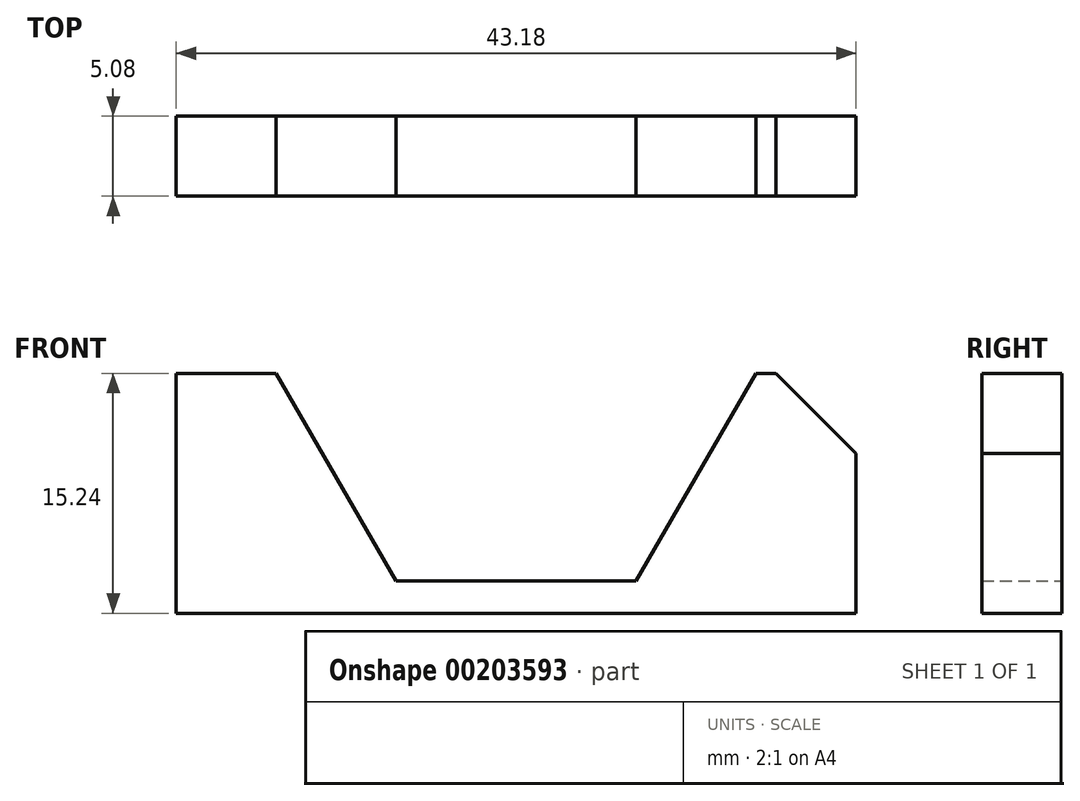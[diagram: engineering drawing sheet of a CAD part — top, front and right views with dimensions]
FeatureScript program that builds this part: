
annotation { "Feature Type Name" : "Feature", "Feature Type Description" : "" }
export const myFeature = defineFeature(function(context is Context, id is Id, definition is map)
    precondition{}
    {
        {
            var Q0;
            Q0=qCreatedBy(makeId("Front.planeOp"),FACE);
            var sketch = newSketch(context, id + "F0", { "sketchPlane" : qUnion([Q0])});
            skLineSegment(sketch, "E0.2", {"start": v(36.83, 0) * mm, "end": v(29.21, -13.2) * mm});
            skLineSegment(sketch, "E0.3", {"start": v(29.21, -13.2) * mm, "end": v(13.97, -13.2) * mm});
            skLineSegment(sketch, "E0.4", {"start": v(13.97, -13.2) * mm, "end": v(6.35, 0) * mm});
            skLineSegment(sketch, "E1", {"start": v(6.35, 0) * mm, "end": v(0, 0) * mm});
            skLineSegment(sketch, "E2", {"start": v(36.83, 0) * mm, "end": v(43.18, 0) * mm});
            skLineSegment(sketch, "E3", {"start": v(43.18, 0) * mm, "end": v(43.18, -15.24) * mm});
            skLineSegment(sketch, "E4", {"start": v(43.18, -15.24) * mm, "end": v(0, -15.24) * mm});
            skLineSegment(sketch, "E5.MirrorCS", {"start": v(-43.18, -15.24) * mm, "end": v(0, -15.24) * mm});
            skLineSegment(sketch, "E6.MirrorCS", {"start": v(-36.83, 0) * mm, "end": v(-43.18, 0) * mm});
            skLineSegment(sketch, "E7.MirrorCS", {"start": v(-6.35, 0) * mm, "end": v(0, 0) * mm});
            skLineSegment(sketch, "E8.MirrorCS", {"start": v(-29.21, -13.2) * mm, "end": v(-13.97, -13.2) * mm});
            skLineSegment(sketch, "E9.MirrorCS", {"start": v(-43.18, 0) * mm, "end": v(-43.18, -15.24) * mm});
            skLineSegment(sketch, "E10.MirrorCS", {"start": v(-36.83, 0) * mm, "end": v(-29.21, -13.2) * mm});
            skLineSegment(sketch, "E11.MirrorCS", {"start": v(-13.97, -13.2) * mm, "end": v(-6.35, 0) * mm});
            skSolve(sketch);
        }
        {
            var Q0;
            Q0=makeQuery(id+"F0.imprint","IMPRINT",FACE,{"disambiguationData":[TD([[makeQuery(id+"F0.imprint","IMPRINT",EDGE,{"derivedFrom":sQuery(id+"F0.wireOp",EDGE,"E0.2")}),1.0]])]});
            extrude(context, id + "F1", {"entities" : qUnion([Q0]), "depth" : 116.84 * mm});
        }
        {
            var Q0;
            Q0=makeQuery(id+"F1.opExtrude","CAP_FACE",FACE,{"disambiguationData":[OSD([sQuery(id+"F0.wireOp",EDGE,"E0.2"),sQuery(id+"F0.wireOp",EDGE,"E0.3"),sQuery(id+"F0.wireOp",EDGE,"E0.4"),sQuery(id+"F0.wireOp",EDGE,"E1"),sQuery(id+"F0.wireOp",EDGE,"E2"),sQuery(id+"F0.wireOp",EDGE,"E3"),sQuery(id+"F0.wireOp",EDGE,"E4"),sQuery(id+"F0.wireOp",EDGE,"E5.MirrorCS"),sQuery(id+"F0.wireOp",EDGE,"E6.MirrorCS"),sQuery(id+"F0.wireOp",EDGE,"E7.MirrorCS"),sQuery(id+"F0.wireOp",EDGE,"E8.MirrorCS"),sQuery(id+"F0.wireOp",EDGE,"E9.MirrorCS"),sQuery(id+"F0.wireOp",EDGE,"E10.MirrorCS"),sQuery(id+"F0.wireOp",EDGE,"E11.MirrorCS")])],"isStart":false});
            var sketch = newSketch(context, id + "F2", { "sketchPlane" : qUnion([Q0])});
            skLineSegment(sketch, "E12.bottom", {"start": v(-43.18, 0) * mm, "end": v(43.18, 0) * mm});
            skLineSegment(sketch, "E12.top", {"start": v(-43.18, -15.24) * mm, "end": v(43.18, -15.24) * mm});
            skLineSegment(sketch, "E12.left", {"start": v(-43.18, 0) * mm, "end": v(-43.18, -15.24) * mm});
            skLineSegment(sketch, "E12.right", {"start": v(43.18, 0) * mm, "end": v(43.18, -15.24) * mm});
            skSolve(sketch);
        }
        {
            var Q0;
            Q0=qSketchRegion(id+"F2",true);
            extrude(context, id + "F3", {"entities" : qUnion([Q0]), "operationType" : NewBodyOperationType.ADD, "depth" : 2.54 * mm});
        }
        {
            var Q0;
            Q0=makeQuery(id+"F1.opExtrude","CAP_FACE",FACE,{"disambiguationData":[OSD([sQuery(id+"F0.wireOp",EDGE,"E0.2"),sQuery(id+"F0.wireOp",EDGE,"E0.3"),sQuery(id+"F0.wireOp",EDGE,"E0.4"),sQuery(id+"F0.wireOp",EDGE,"E1"),sQuery(id+"F0.wireOp",EDGE,"E2"),sQuery(id+"F0.wireOp",EDGE,"E3"),sQuery(id+"F0.wireOp",EDGE,"E4"),sQuery(id+"F0.wireOp",EDGE,"E5.MirrorCS"),sQuery(id+"F0.wireOp",EDGE,"E6.MirrorCS"),sQuery(id+"F0.wireOp",EDGE,"E7.MirrorCS"),sQuery(id+"F0.wireOp",EDGE,"E8.MirrorCS"),sQuery(id+"F0.wireOp",EDGE,"E9.MirrorCS"),sQuery(id+"F0.wireOp",EDGE,"E10.MirrorCS"),sQuery(id+"F0.wireOp",EDGE,"E11.MirrorCS")])],"isStart":true});
            var sketch = newSketch(context, id + "F4", { "sketchPlane" : qUnion([Q0])});
            skLineSegment(sketch, "E13.bottom", {"start": v(-43.18, 0) * mm, "end": v(43.18, 0) * mm});
            skLineSegment(sketch, "E13.top", {"start": v(-43.18, -15.24) * mm, "end": v(43.18, -15.24) * mm});
            skLineSegment(sketch, "E13.left", {"start": v(-43.18, 0) * mm, "end": v(-43.18, -15.24) * mm});
            skLineSegment(sketch, "E13.right", {"start": v(43.18, 0) * mm, "end": v(43.18, -15.24) * mm});
            skSolve(sketch);
        }
        {
            var Q0;
            Q0=qSketchRegion(id+"F4",true);
            extrude(context, id + "F5", {"entities" : qUnion([Q0]), "operationType" : NewBodyOperationType.ADD, "depth" : 2.54 * mm});
        }
        {
            var Q0;
            Q0=makeQuery(id+"F5.boolean.opBoolean","MERGE",EDGE,{"derivedFrom":[makeQuery(id+"F3.boolean.opBoolean","MERGE",EDGE,{"derivedFrom":[makeQuery(id+"F1.opExtrude","SWEPT_EDGE",EDGE,{"disambiguationData":[OSD([sQuery(id+"F0.wireOp",EDGE,"E6.MirrorCS"),sQuery(id+"F0.wireOp",EDGE,"E9.MirrorCS")])]}),makeQuery(id+"F3.opExtrude","SWEPT_EDGE",EDGE,{"disambiguationData":[OSD([sQuery(id+"F2.wireOp",EDGE,"E12.bottom"),sQuery(id+"F2.wireOp",EDGE,"E12.left")])]})]}),makeQuery(id+"F5.opExtrude","SWEPT_EDGE",EDGE,{"disambiguationData":[OSD([sQuery(id+"F4.wireOp",EDGE,"E13.bottom"),sQuery(id+"F4.wireOp",EDGE,"E13.right")])]})]});
            var Q1;
            Q1=makeQuery(id+"F3.opExtrude","CAP_EDGE",EDGE,{"disambiguationData":[OSD([sQuery(id+"F2.wireOp",EDGE,"E12.bottom")])],"isStart":false});
            var Q2;
            Q2=makeQuery(id+"F5.boolean.opBoolean","MERGE",EDGE,{"derivedFrom":[makeQuery(id+"F3.boolean.opBoolean","MERGE",EDGE,{"derivedFrom":[makeQuery(id+"F1.opExtrude","SWEPT_EDGE",EDGE,{"disambiguationData":[OSD([sQuery(id+"F0.wireOp",EDGE,"E2"),sQuery(id+"F0.wireOp",EDGE,"E3")])]}),makeQuery(id+"F3.opExtrude","SWEPT_EDGE",EDGE,{"disambiguationData":[OSD([sQuery(id+"F2.wireOp",EDGE,"E12.bottom"),sQuery(id+"F2.wireOp",EDGE,"E12.right")])]})]}),makeQuery(id+"F5.opExtrude","SWEPT_EDGE",EDGE,{"disambiguationData":[OSD([sQuery(id+"F4.wireOp",EDGE,"E13.bottom"),sQuery(id+"F4.wireOp",EDGE,"E13.left")])]})]});
            var Q3;
            Q3=makeQuery(id+"F5.opExtrude","CAP_EDGE",EDGE,{"disambiguationData":[OSD([sQuery(id+"F4.wireOp",EDGE,"E13.bottom")])],"isStart":false});
            chamfer(context, id + "F6", {"entities" : qUnion([Q0, Q1, Q2, Q3]), "width" : 5.08 * mm, "tangentPropagation" : true});
        }
        {
            var Q0;
            Q0=makeQuery(id+"F3.opExtrude","CAP_EDGE",EDGE,{"disambiguationData":[OSD([sQuery(id+"F2.wireOp",EDGE,"E12.left")])],"isStart":false});
            var Q1;
            Q1=makeQuery(id+"F3.opExtrude","CAP_EDGE",EDGE,{"disambiguationData":[OSD([sQuery(id+"F2.wireOp",EDGE,"E12.right")])],"isStart":false});
            var Q2;
            Q2=makeQuery(id+"F5.opExtrude","CAP_EDGE",EDGE,{"disambiguationData":[OSD([sQuery(id+"F4.wireOp",EDGE,"E13.left")])],"isStart":false});
            var Q3;
            Q3=makeQuery(id+"F5.opExtrude","CAP_EDGE",EDGE,{"disambiguationData":[OSD([sQuery(id+"F4.wireOp",EDGE,"E13.right")])],"isStart":false});
            chamfer(context, id + "F7", {"entities" : qUnion([Q0, Q1, Q2, Q3]), "width" : 5.08 * mm, "tangentPropagation" : true});
        }
        {
            var Q0;
            Q0=makeQuery(id+"F3.opExtrude","CAP_FACE",FACE,{"disambiguationData":[OSD([sQuery(id+"F2.wireOp",EDGE,"E12.bottom"),sQuery(id+"F2.wireOp",EDGE,"E12.top"),sQuery(id+"F2.wireOp",EDGE,"E12.left"),sQuery(id+"F2.wireOp",EDGE,"E12.right")])],"isStart":false});
            var sketch = newSketch(context, id + "F8", { "sketchPlane" : qUnion([Q0])});
            skLineSegment(sketch, "E14.bottom", {"start": v(-46.5, 10.22) * mm, "end": v(45.28, 10.22) * mm});
            skLineSegment(sketch, "E14.top", {"start": v(-46.5, -20.03) * mm, "end": v(45.28, -20.03) * mm});
            skLineSegment(sketch, "E14.left", {"start": v(-46.5, 10.22) * mm, "end": v(-46.5, -20.03) * mm});
            skLineSegment(sketch, "E14.right", {"start": v(45.28, 10.22) * mm, "end": v(45.28, -20.03) * mm});
            skSolve(sketch);
        }
        {
            var Q0;
            Q0 = qSketchRegion(id + "F8", true);
            extrude(context, id + "F9", {"entities" : qUnion([Q0]), "operationType" : NewBodyOperationType.REMOVE, "oppositeDirection" : true, "depth" : 106.68 * mm});
        }
        {
            var Q0;
            Q0=makeQuery(id+"F5.opExtrude","CAP_FACE",FACE,{"disambiguationData":[OSD([sQuery(id+"F4.wireOp",EDGE,"E13.bottom"),sQuery(id+"F4.wireOp",EDGE,"E13.top"),sQuery(id+"F4.wireOp",EDGE,"E13.left"),sQuery(id+"F4.wireOp",EDGE,"E13.right")])],"isStart":false});
            var sketch = newSketch(context, id + "F10", { "sketchPlane" : qUnion([Q0])});
            skLineSegment(sketch, "E15.bottom", {"start": v(-48.32, 5.02) * mm, "end": v(50.96, 5.02) * mm});
            skLineSegment(sketch, "E15.top", {"start": v(-48.32, -20.33) * mm, "end": v(50.96, -20.33) * mm});
            skLineSegment(sketch, "E15.left", {"start": v(-48.32, 5.02) * mm, "end": v(-48.32, -20.33) * mm});
            skLineSegment(sketch, "E15.right", {"start": v(50.96, 5.02) * mm, "end": v(50.96, -20.33) * mm});
            skSolve(sketch);
        }
        {
            var Q0;
            Q0 = qSketchRegion(id + "F10", true);
            extrude(context, id + "F11", {"entities" : qUnion([Q0]), "operationType" : NewBodyOperationType.REMOVE, "oppositeDirection" : true, "depth" : 10.16 * mm});
        }
        {
            var Q0;
            Q0=makeQuery(id+"F5.boolean.opBoolean","MERGE",FACE,{"derivedFrom":[makeQuery(id+"F3.boolean.opBoolean","MERGE",FACE,{"derivedFrom":[makeQuery(id+"F1.opExtrude","SWEPT_FACE",FACE,{"disambiguationData":[OSD([sQuery(id+"F0.wireOp",EDGE,"E9.MirrorCS")])]}),makeQuery(id+"F3.opExtrude","SWEPT_FACE",FACE,{"disambiguationData":[OSD([sQuery(id+"F2.wireOp",EDGE,"E12.left")])]})]}),makeQuery(id+"F5.opExtrude","SWEPT_FACE",FACE,{"disambiguationData":[OSD([sQuery(id+"F4.wireOp",EDGE,"E13.right")])]})]});
            var sketch = newSketch(context, id + "F12", { "sketchPlane" : qUnion([Q0])});
            skLineSegment(sketch, "E16.bottom", {"start": v(2.84, 3) * mm, "end": v(18.17, 3) * mm});
            skLineSegment(sketch, "E16.top", {"start": v(2.84, -18.3) * mm, "end": v(18.17, -18.3) * mm});
            skLineSegment(sketch, "E16.left", {"start": v(2.84, 3) * mm, "end": v(2.84, -18.3) * mm});
            skLineSegment(sketch, "E16.right", {"start": v(18.17, 3) * mm, "end": v(18.17, -18.3) * mm});
            skSolve(sketch);
        }
        {
            var Q0;
            Q0 = qSketchRegion(id + "F12", true);
            extrude(context, id + "F13", {"entities" : qUnion([Q0]), "operationType" : NewBodyOperationType.REMOVE, "oppositeDirection" : true, "depth" : 43.18 * mm});
        }
    });
